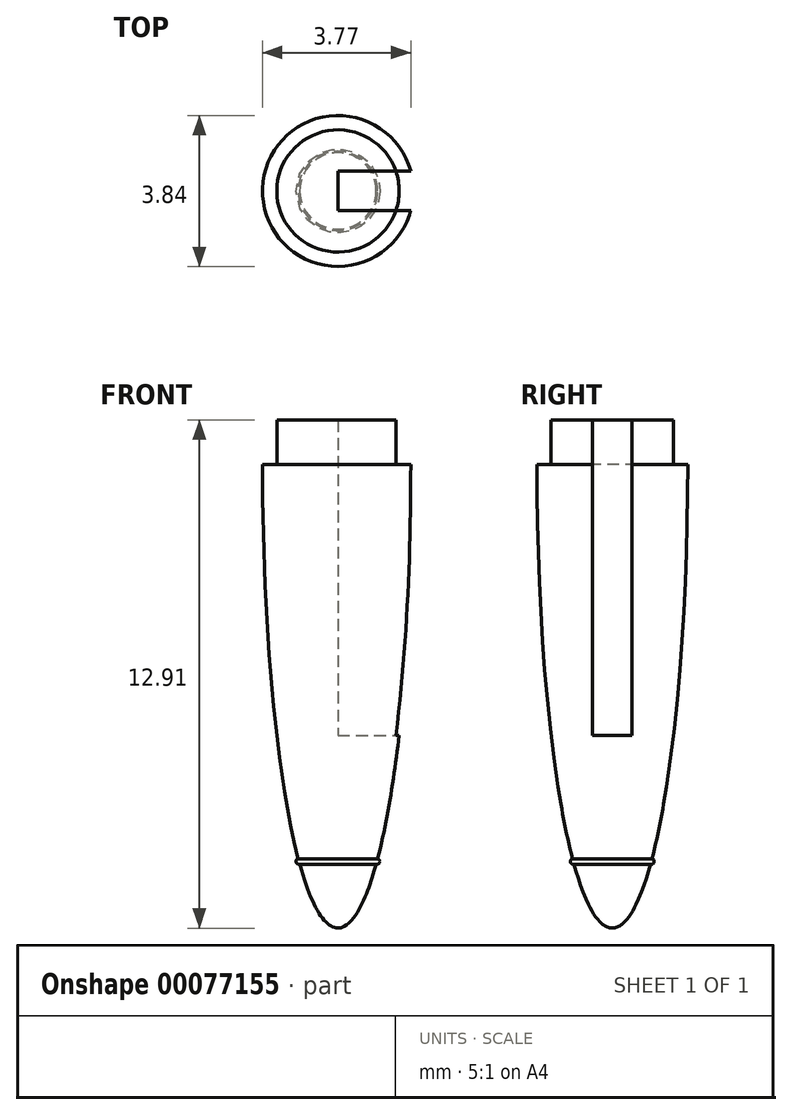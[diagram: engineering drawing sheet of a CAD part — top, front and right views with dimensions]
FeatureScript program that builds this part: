
annotation { "Feature Type Name" : "Feature", "Feature Type Description" : "" }
export const myFeature = defineFeature(function(context is Context, id is Id, definition is map)
    precondition{}
    {
        {
            var Q0;
            Q0=qCreatedBy(makeId("Front.planeOp"),FACE);
            var sketch = newSketch(context, id + "F0", { "sketchPlane" : qUnion([Q0])});
            skEllipticalArc(sketch, "E0", {});
            skLineSegment(sketch, "E1", {"start": v(0, 11.78) * mm, "end": v(0, -11.78) * mm});
            skLineSegment(sketch, "E2.bottom", {"start": v(-0.43, 11.48) * mm, "end": v(-0.43, 11.48) * mm});
            skLineSegment(sketch, "E2.top", {"start": v(-0.42, 12.66) * mm, "end": v(-0.43, 12.66) * mm});
            skLineSegment(sketch, "E2.left", {"start": v(0, 11.48) * mm, "end": v(0, 12.66) * mm});
            skLineSegment(sketch, "E2.right", {"start": v(-0.43, 11.48) * mm, "end": v(-0.43, 12.66) * mm});
            skLineSegment(sketch, "E3.left", {"start": v(0, 12.66) * mm, "end": v(0, 14.78) * mm});
            skLineSegment(sketch, "E3.right", {"start": v(-0.42, 12.66) * mm, "end": v(-0.42, 14.78) * mm});
            skLineSegment(sketch, "E4.left", {"start": v(0, 14.78) * mm, "end": v(0, 16.48) * mm});
            skLineSegment(sketch, "E4.right", {"start": v(-0.3, 14.78) * mm, "end": v(-0.3, 16.48) * mm});
            skLineSegment(sketch, "E5", {"start": v(-0.3, 14.78) * mm, "end": v(-0.42, 14.78) * mm});
            skArc(sketch, "E6", {"start": v(-0.68, 11) * mm, "mid": v(-0.78, 10.97) * mm, "end": v(-0.74, 10.87) * mm});
            skEllipticalArc(sketch, "E7.trimOffspring", {});
            skArc(sketch, "E8", {"start": v(-1, -10.01) * mm, "mid": v(-1.06, -10.1) * mm, "end": v(-0.97, -10.16) * mm});
            skEllipticalArc(sketch, "E9.trimOffspring", {});
            skLineSegment(sketch, "E10.bottom", {"start": v(-0.3, 16.48) * mm, "end": v(-0.52, 16.48) * mm});
            skLineSegment(sketch, "E10.top", {"start": v(0, 16.77) * mm, "end": v(-0.52, 16.77) * mm});
            skLineSegment(sketch, "E10.left", {"start": v(0, 16.48) * mm, "end": v(0, 16.77) * mm});
            skLineSegment(sketch, "E10.right", {"start": v(-0.52, 16.48) * mm, "end": v(-0.52, 16.77) * mm});
            const initialGuessF0  = {"E0": [0, 0, 0, 1, 0.011777514631263973, 0.001916683178784572, 0.22421039553335678, 0.36366982071250753], "E7.trimOffspring": [0, 0, 0, 1, 0.011777514631263973, 0.001916683178784572, 0.3950853549318617, 2.587374773479048], "E9.trimOffspring": [0, 0, 0, 1, 0.011777514631263973, 0.001916683178784572, 2.6108752879956154, 3.141592653589793]};
            skSetInitialGuess(sketch, initialGuessF0);
            skSolve(sketch);
        }
        {
            var Q0;
            Q0=makeQuery(id+"F0.imprint","IMPRINT",FACE,{"disambiguationData":[TD([[makeQuery(id+"F0.imprint","IMPRINT",EDGE,{"derivedFrom":sQuery(id+"F0.wireOp",EDGE,"E0")}),1.0]])]});
            var Q1;
            Q1=sQuery(id+"F0.wireOp",EDGE,"E1");
            revolve(context, id + "F1", {"entities" : qUnion([Q0]), "axis" : qUnion([Q1]), "revolveType" : RevolveType.FULL});
        }
        {
            var Q0;
            Q0=qCreatedBy(makeId("Front.planeOp"),FACE);
            var sketch = newSketch(context, id + "F2", { "sketchPlane" : qUnion([Q0])});
            skLineSegment(sketch, "E11.bottom", {"start": v(-5.29, 0) * mm, "end": v(9.51, 0) * mm});
            skLineSegment(sketch, "E11.top", {"start": v(-5.29, 17.48) * mm, "end": v(9.51, 17.48) * mm});
            skLineSegment(sketch, "E11.left", {"start": v(-5.29, 0) * mm, "end": v(-5.29, 17.48) * mm});
            skLineSegment(sketch, "E11.right", {"start": v(9.51, 0) * mm, "end": v(9.51, 17.48) * mm});
            skSolve(sketch);
        }
        {
            var Q0;
            Q0=makeQuery(id+"F2.imprint","IMPRINT",FACE,{"disambiguationData":[TD([[makeQuery(id+"F2.imprint","IMPRINT",EDGE,{"derivedFrom":sQuery(id+"F2.wireOp",EDGE,"E11.bottom")}),1.0]])]});
            extrude(context, id + "F3", {"entities" : qUnion([Q0]), "operationType" : NewBodyOperationType.REMOVE, "depth" : 25 * mm, "offsetDistance" : 25 * mm, "symmetric" : true});
        }
        {
            var Q0;
            Q0=qCreatedBy(makeId("Front.planeOp"),FACE);
            var sketch = newSketch(context, id + "F4", { "sketchPlane" : qUnion([Q0])});
            skLineSegment(sketch, "E12.top", {"start": v(0, 1.13) * mm, "end": v(-1.55, 1.13) * mm});
            skLineSegment(sketch, "E12.left", {"start": v(0, 0) * mm, "end": v(0, 1.13) * mm});
            skLineSegment(sketch, "E12.right", {"start": v(-1.55, 0) * mm, "end": v(-1.55, 1.13) * mm});
            skLineSegment(sketch, "E13.MirrorCS", {"start": v(-1.55, 0) * mm, "end": v(-1.55, -1.13) * mm});
            skLineSegment(sketch, "E14.MirrorCS", {"start": v(0, -1.13) * mm, "end": v(-1.55, -1.13) * mm});
            skLineSegment(sketch, "E15.MirrorCS", {"start": v(0, 0) * mm, "end": v(0, -1.13) * mm});
            skSolve(sketch);
        }
        {
            var Q0;
            Q0=qCreatedBy(makeId("Front.planeOp"),FACE);
            var sketch = newSketch(context, id + "F5", { "sketchPlane" : qUnion([Q0])});
            skLineSegment(sketch, "E16.bottom", {"start": v(0, 7.17) * mm, "end": v(4.16, 7.17) * mm});
            skLineSegment(sketch, "E16.top", {"start": v(0, -6.88) * mm, "end": v(4.16, -6.88) * mm});
            skLineSegment(sketch, "E16.left", {"start": v(0, 7.17) * mm, "end": v(0, -6.88) * mm});
            skLineSegment(sketch, "E16.right", {"start": v(4.16, 7.17) * mm, "end": v(4.16, -6.88) * mm});
            skSolve(sketch);
        }
        {
            var Q0;
            Q0=qSketchRegion(id+"F4",true);
            var Q1;
            Q1=sQuery(id+"F4.wireOp",EDGE,"E15.MirrorCS");
            revolve(context, id + "F6", {"operationType" : NewBodyOperationType.ADD, "entities" : qUnion([Q0]), "axis" : qUnion([Q1]), "revolveType" : RevolveType.FULL, "oppositeDirection" : true});
        }
        {
            var Q0;
            Q0=makeQuery(id+"F5.imprint","IMPRINT",FACE,{"disambiguationData":[TD([[makeQuery(id+"F5.imprint","IMPRINT",EDGE,{"derivedFrom":sQuery(id+"F5.wireOp",EDGE,"E16.bottom")}),-1.0]])]});
            extrude(context, id + "F7", {"entities" : qUnion([Q0]), "operationType" : NewBodyOperationType.REMOVE, "depth" : 1 * mm, "offsetDistance" : 25 * mm, "symmetric" : true});
        }
    });
